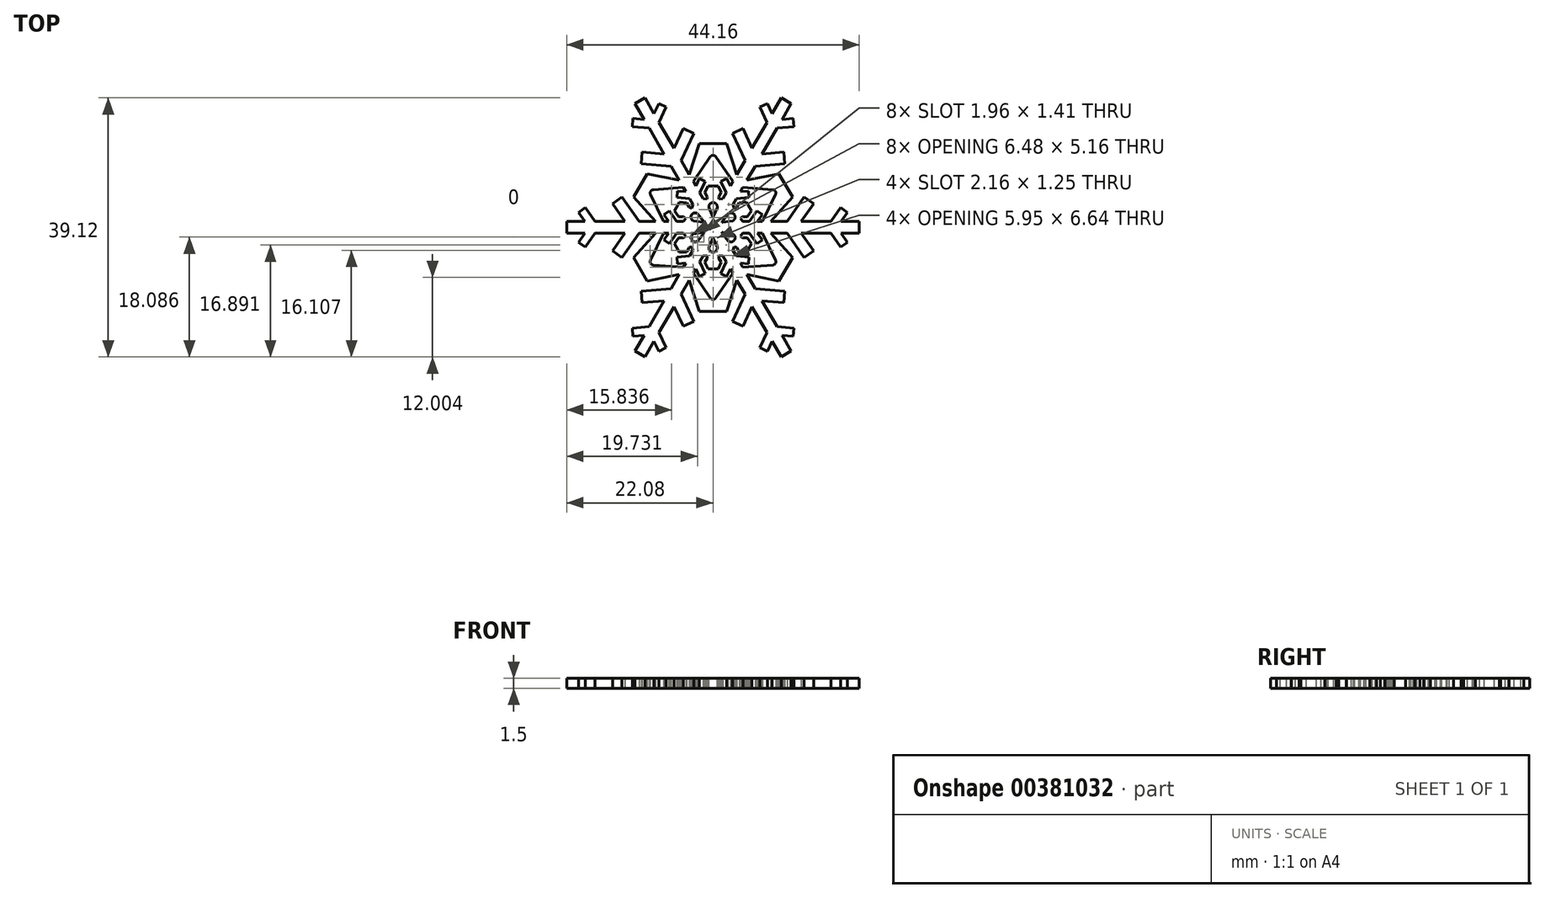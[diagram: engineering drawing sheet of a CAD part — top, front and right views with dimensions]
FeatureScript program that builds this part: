
annotation { "Feature Type Name" : "Feature", "Feature Type Description" : "" }
export const myFeature = defineFeature(function(context is Context, id is Id, definition is map)
    precondition{}
    {
        {
            var Q0;
            Q0=qCreatedBy(makeId("Top.planeOp"),FACE);
            var sketch = newSketch(context, id + "F0", { "sketchPlane" : qUnion([Q0])});
            skLineSegment(sketch, "E0.bottom", {"start": v(-43.7, 44.8) * mm, "end": v(41.1, 44.8) * mm});
            skLineSegment(sketch, "E0.top", {"start": v(-43.7, -40) * mm, "end": v(41.1, -40) * mm});
            skLineSegment(sketch, "E0.left", {"start": v(-43.7, 44.8) * mm, "end": v(-43.7, -40) * mm});
            skLineSegment(sketch, "E0.right", {"start": v(41.1, 44.8) * mm, "end": v(41.1, -40) * mm});
            skLineSegment(sketch, "E1", {"start": v(-44.15, 0) * mm, "end": v(-44.15, 1.75) * mm});
            skLineSegment(sketch, "E2", {"start": v(-44.15, 1.75) * mm, "end": v(-38.65, 1.75) * mm});
            skLineSegment(sketch, "E3", {"start": v(-38.65, 1.75) * mm, "end": v(-40.58, 4.5) * mm});
            skLineSegment(sketch, "E4", {"start": v(-40.58, 4.5) * mm, "end": v(-38.53, 5.94) * mm});
            skLineSegment(sketch, "E5", {"start": v(-38.53, 5.94) * mm, "end": v(-35.6, 1.75) * mm});
            skLineSegment(sketch, "E6", {"start": v(-35.6, 1.75) * mm, "end": v(-26.6, 1.75) * mm});
            skLineSegment(sketch, "E7", {"start": v(-26.6, 1.75) * mm, "end": v(-30.36, 7.13) * mm});
            skLineSegment(sketch, "E8", {"start": v(-30.36, 7.13) * mm, "end": v(-27.49, 9.13) * mm});
            skLineSegment(sketch, "E9", {"start": v(-27.49, 9.13) * mm, "end": v(-22.34, 1.75) * mm});
            skLineSegment(sketch, "E10", {"start": v(-22.34, 1.75) * mm, "end": v(-17.4, 1.75) * mm});
            skLineSegment(sketch, "E11", {"start": v(-14.94, 1.75) * mm, "end": v(-13.44, 1.75) * mm});
            skLineSegment(sketch, "E12", {"start": v(-13.44, 1.75) * mm, "end": v(-14.87, 3.8) * mm});
            skLineSegment(sketch, "E13", {"start": v(-14.87, 3.8) * mm, "end": v(-13.23, 4.94) * mm});
            skLineSegment(sketch, "E14", {"start": v(-13.23, 4.94) * mm, "end": v(-11, 1.75) * mm});
            skLineSegment(sketch, "E15", {"start": v(0, 0) * mm, "end": v(-44.15, 0) * mm, "construction": true});
            skLineSegment(sketch, "E16", {"start": v(-11, 1.75) * mm, "end": v(-8.98, 1.75) * mm});
            skLineSegment(sketch, "E17", {"start": v(0, 0) * mm, "end": v(-10.85, 6.27) * mm});
            skLineSegment(sketch, "E18", {"start": v(-8.98, 1.75) * mm, "end": v(-8.24, 2.67) * mm});
            skLineSegment(sketch, "E19", {"start": v(-8.24, 2.67) * mm, "end": v(-8.84, 3.15) * mm});
            skLineSegment(sketch, "E20", {"start": v(-8.84, 3.15) * mm, "end": v(-10.37, 3.15) * mm});
            skLineSegment(sketch, "E21", {"start": v(-10.37, 3.15) * mm, "end": v(-11.62, 4.94) * mm});
            skLineSegment(sketch, "E22", {"start": v(-11.62, 4.94) * mm, "end": v(-10.85, 6.27) * mm});
            skLineSegment(sketch, "E23", {"start": v(-10.85, 6.27) * mm, "end": v(-31.84, 18.38) * mm, "construction": true});
            skLineSegment(sketch, "E24", {"start": v(-23.98, 9.13) * mm, "end": v(-21.94, 12.67) * mm});
            skLineSegment(sketch, "E25", {"start": v(-14.94, 1.75) * mm, "end": v(-19.5, 11.26) * mm});
            skLineSegment(sketch, "E26", {"start": v(-23.98, 9.13) * mm, "end": v(-17.4, 1.75) * mm});
            skLineSegment(sketch, "E27", {"start": v(-21.94, 12.67) * mm, "end": v(-19.5, 11.26) * mm});
            skLineSegment(sketch, "E28.MirrorCS", {"start": v(0, 0) * mm, "end": v(-10.85, -6.27) * mm});
            skLineSegment(sketch, "E29.MirrorCS", {"start": v(-44.15, 0) * mm, "end": v(-44.15, -1.75) * mm});
            skLineSegment(sketch, "E30.MirrorCS", {"start": v(-14.94, -1.75) * mm, "end": v(-13.44, -1.75) * mm});
            skLineSegment(sketch, "E31.MirrorCS", {"start": v(-11.62, -4.94) * mm, "end": v(-10.85, -6.27) * mm});
            skLineSegment(sketch, "E32.MirrorCS", {"start": v(-14.87, -3.8) * mm, "end": v(-13.23, -4.94) * mm});
            skLineSegment(sketch, "E33.MirrorCS", {"start": v(-8.98, -1.75) * mm, "end": v(-8.24, -2.67) * mm});
            skLineSegment(sketch, "E34.MirrorCS", {"start": v(-8.84, -3.15) * mm, "end": v(-10.37, -3.15) * mm});
            skLineSegment(sketch, "E35.MirrorCS", {"start": v(-8.24, -2.67) * mm, "end": v(-8.84, -3.15) * mm});
            skLineSegment(sketch, "E36.MirrorCS", {"start": v(-14.94, -1.75) * mm, "end": v(-19.5, -11.26) * mm});
            skLineSegment(sketch, "E37.MirrorCS", {"start": v(-27.49, -9.13) * mm, "end": v(-22.34, -1.75) * mm});
            skLineSegment(sketch, "E38.MirrorCS", {"start": v(-21.94, -12.67) * mm, "end": v(-19.5, -11.26) * mm});
            skLineSegment(sketch, "E39.MirrorCS", {"start": v(-23.98, -9.13) * mm, "end": v(-21.94, -12.67) * mm});
            skLineSegment(sketch, "E40.MirrorCS", {"start": v(-11, -1.75) * mm, "end": v(-8.98, -1.75) * mm});
            skLineSegment(sketch, "E41.MirrorCS", {"start": v(-38.53, -5.94) * mm, "end": v(-35.6, -1.75) * mm});
            skLineSegment(sketch, "E42.MirrorCS", {"start": v(-40.58, -4.5) * mm, "end": v(-38.53, -5.94) * mm});
            skLineSegment(sketch, "E43.MirrorCS", {"start": v(-38.65, -1.75) * mm, "end": v(-40.58, -4.5) * mm});
            skLineSegment(sketch, "E44.MirrorCS", {"start": v(-44.15, -1.75) * mm, "end": v(-38.65, -1.75) * mm});
            skLineSegment(sketch, "E45.MirrorCS", {"start": v(-23.98, -9.13) * mm, "end": v(-17.4, -1.75) * mm});
            skLineSegment(sketch, "E46.MirrorCS", {"start": v(-30.36, -7.13) * mm, "end": v(-27.49, -9.13) * mm});
            skLineSegment(sketch, "E47.MirrorCS", {"start": v(-26.6, -1.75) * mm, "end": v(-30.36, -7.13) * mm});
            skLineSegment(sketch, "E48.MirrorCS", {"start": v(-35.6, -1.75) * mm, "end": v(-26.6, -1.75) * mm});
            skLineSegment(sketch, "E49.MirrorCS", {"start": v(-22.34, -1.75) * mm, "end": v(-17.4, -1.75) * mm});
            skLineSegment(sketch, "E50.MirrorCS", {"start": v(-13.44, -1.75) * mm, "end": v(-14.87, -3.8) * mm});
            skLineSegment(sketch, "E51.MirrorCS", {"start": v(-10.37, -3.15) * mm, "end": v(-11.62, -4.94) * mm});
            skLineSegment(sketch, "E52.MirrorCS", {"start": v(-13.23, -4.94) * mm, "end": v(-11, -1.75) * mm});
            skSolve(sketch);
        }
        {
            var Q0;
            Q0=makeQuery(id+"F0.imprint","IMPRINT",FACE,{"disambiguationData":[TD([[makeQuery(id+"F0.imprint","IMPRINT",EDGE,{"derivedFrom":sQuery(id+"F0.wireOp",EDGE,"E1")}),-1.0]])]});
            var Q1;
            {var subQ0=sQuery(id+"F0.wireOp",EDGE,"E3");Q1=makeQuery(id+"F0.imprint","IMPRINT",FACE,{"disambiguationData":[TD([[makeQuery(id+"F0.imprint","IMPRINT",EDGE,{"derivedFrom":subQ0}),-1.0]])]});}
            extrude(context, id + "F1", {"entities" : qUnion([Q0, Q1]), "endBound" : BoundingType.SYMMETRIC, "depth" : 3 * mm});
        }
        {
            var Q0;
            Q0=qCreatedBy(makeId("Right.planeOp"),FACE);
            var sketch = newSketch(context, id + "F2", { "sketchPlane" : qUnion([Q0])});
            skLineSegment(sketch, "E53", {"start": v(0, 0) * mm, "end": v(0, -43.45) * mm, "construction": true});
            skSolve(sketch);
        }
        {
            var Q0;
            Q0=makeQuery(id+"F1.opExtrude","SWEPT_BODY",BODY,{"disambiguationData":[OSD([sQuery(id+"F0.wireOp",EDGE,"E1"),sQuery(id+"F0.wireOp",EDGE,"E2"),sQuery(id+"F0.wireOp",EDGE,"E3"),sQuery(id+"F0.wireOp",EDGE,"E4"),sQuery(id+"F0.wireOp",EDGE,"E5"),sQuery(id+"F0.wireOp",EDGE,"E6"),sQuery(id+"F0.wireOp",EDGE,"E7"),sQuery(id+"F0.wireOp",EDGE,"E8"),sQuery(id+"F0.wireOp",EDGE,"E9"),sQuery(id+"F0.wireOp",EDGE,"E10"),sQuery(id+"F0.wireOp",EDGE,"189a7a4e-f39c-4bfd-b122-43a29ca94680"),sQuery(id+"F0.wireOp",EDGE,"67050dc1-3990-4a49-9707-dffdccfb30a0"),sQuery(id+"F0.wireOp",EDGE,"437a0215-fb6c-4063-ad75-b84b83856d58"),sQuery(id+"F0.wireOp",EDGE,"E11"),sQuery(id+"F0.wireOp",EDGE,"E12"),sQuery(id+"F0.wireOp",EDGE,"E13"),sQuery(id+"F0.wireOp",EDGE,"E14"),sQuery(id+"F0.wireOp",EDGE,"5e9898c1-a996-4e9f-834a-20b7154747a1"),sQuery(id+"F0.wireOp",EDGE,"4f175b08-8b9f-4015-be58-81c3dce13333"),sQuery(id+"F0.wireOp",EDGE,"3166d6ec-2b74-46b0-8a25-8ff819b97b050.MirrorCS"),sQuery(id+"F0.wireOp",EDGE,"3166d6ec-2b74-46b0-8a25-8ff819b97b051.MirrorCS"),sQuery(id+"F0.wireOp",EDGE,"3166d6ec-2b74-46b0-8a25-8ff819b97b052.MirrorCS"),sQuery(id+"F0.wireOp",EDGE,"3166d6ec-2b74-46b0-8a25-8ff819b97b053.MirrorCS"),sQuery(id+"F0.wireOp",EDGE,"3166d6ec-2b74-46b0-8a25-8ff819b97b054.MirrorCS"),sQuery(id+"F0.wireOp",EDGE,"3166d6ec-2b74-46b0-8a25-8ff819b97b055.MirrorCS"),sQuery(id+"F0.wireOp",EDGE,"3166d6ec-2b74-46b0-8a25-8ff819b97b056.MirrorCS"),sQuery(id+"F0.wireOp",EDGE,"3166d6ec-2b74-46b0-8a25-8ff819b97b057.MirrorCS"),sQuery(id+"F0.wireOp",EDGE,"3166d6ec-2b74-46b0-8a25-8ff819b97b058.MirrorCS"),sQuery(id+"F0.wireOp",EDGE,"3166d6ec-2b74-46b0-8a25-8ff819b97b059.MirrorCS"),sQuery(id+"F0.wireOp",EDGE,"3166d6ec-2b74-46b0-8a25-8ff819b97b0510.MirrorCS"),sQuery(id+"F0.wireOp",EDGE,"3166d6ec-2b74-46b0-8a25-8ff819b97b0511.MirrorCS"),sQuery(id+"F0.wireOp",EDGE,"3166d6ec-2b74-46b0-8a25-8ff819b97b0512.MirrorCS"),sQuery(id+"F0.wireOp",EDGE,"3166d6ec-2b74-46b0-8a25-8ff819b97b0513.MirrorCS"),sQuery(id+"F0.wireOp",EDGE,"3166d6ec-2b74-46b0-8a25-8ff819b97b0514.MirrorCS"),sQuery(id+"F0.wireOp",EDGE,"3166d6ec-2b74-46b0-8a25-8ff819b97b0515.MirrorCS"),sQuery(id+"F0.wireOp",EDGE,"3166d6ec-2b74-46b0-8a25-8ff819b97b0516.MirrorCS"),sQuery(id+"F0.wireOp",EDGE,"3166d6ec-2b74-46b0-8a25-8ff819b97b0517.MirrorCS"),sQuery(id+"F0.wireOp",EDGE,"3166d6ec-2b74-46b0-8a25-8ff819b97b0518.MirrorCS")])]});
            var Q1;
            Q1=sQuery(id+"F2.wireOp",EDGE,"E53");
            circularPattern(context, id + "F3", {"operationType" : NewBodyOperationType.ADD, "entities" : qUnion([Q0]), "axis" : qUnion([Q1]), "angle" : 60 * degree, "instanceCount" : 6});
        }
        {
            var Q0;
            {var subQ0=makeQuery(id+"F1.opExtrude","CAP_FACE",FACE,{"disambiguationData":[OSD([sQuery(id+"F0.wireOp",EDGE,"E1"),sQuery(id+"F0.wireOp",EDGE,"E2"),sQuery(id+"F0.wireOp",EDGE,"E3"),sQuery(id+"F0.wireOp",EDGE,"E4"),sQuery(id+"F0.wireOp",EDGE,"E5"),sQuery(id+"F0.wireOp",EDGE,"E6"),sQuery(id+"F0.wireOp",EDGE,"E7"),sQuery(id+"F0.wireOp",EDGE,"E8"),sQuery(id+"F0.wireOp",EDGE,"E9"),sQuery(id+"F0.wireOp",EDGE,"E10"),sQuery(id+"F0.wireOp",EDGE,"189a7a4e-f39c-4bfd-b122-43a29ca94680"),sQuery(id+"F0.wireOp",EDGE,"67050dc1-3990-4a49-9707-dffdccfb30a0"),sQuery(id+"F0.wireOp",EDGE,"437a0215-fb6c-4063-ad75-b84b83856d58"),sQuery(id+"F0.wireOp",EDGE,"E11"),sQuery(id+"F0.wireOp",EDGE,"E12"),sQuery(id+"F0.wireOp",EDGE,"E13"),sQuery(id+"F0.wireOp",EDGE,"E14"),sQuery(id+"F0.wireOp",EDGE,"E16"),sQuery(id+"F0.wireOp",EDGE,"E17"),sQuery(id+"F0.wireOp",EDGE,"E18"),sQuery(id+"F0.wireOp",EDGE,"E19"),sQuery(id+"F0.wireOp",EDGE,"E20"),sQuery(id+"F0.wireOp",EDGE,"E21"),sQuery(id+"F0.wireOp",EDGE,"E22"),sQuery(id+"F0.wireOp",EDGE,"0c32c283-354d-45ec-8926-575daeb4bd260.MirrorCS"),sQuery(id+"F0.wireOp",EDGE,"0c32c283-354d-45ec-8926-575daeb4bd261.MirrorCS"),sQuery(id+"F0.wireOp",EDGE,"0c32c283-354d-45ec-8926-575daeb4bd262.MirrorCS"),sQuery(id+"F0.wireOp",EDGE,"0c32c283-354d-45ec-8926-575daeb4bd263.MirrorCS"),sQuery(id+"F0.wireOp",EDGE,"0c32c283-354d-45ec-8926-575daeb4bd264.MirrorCS"),sQuery(id+"F0.wireOp",EDGE,"0c32c283-354d-45ec-8926-575daeb4bd265.MirrorCS"),sQuery(id+"F0.wireOp",EDGE,"0c32c283-354d-45ec-8926-575daeb4bd266.MirrorCS"),sQuery(id+"F0.wireOp",EDGE,"0c32c283-354d-45ec-8926-575daeb4bd267.MirrorCS"),sQuery(id+"F0.wireOp",EDGE,"0c32c283-354d-45ec-8926-575daeb4bd268.MirrorCS"),sQuery(id+"F0.wireOp",EDGE,"0c32c283-354d-45ec-8926-575daeb4bd269.MirrorCS"),sQuery(id+"F0.wireOp",EDGE,"0c32c283-354d-45ec-8926-575daeb4bd2610.MirrorCS"),sQuery(id+"F0.wireOp",EDGE,"0c32c283-354d-45ec-8926-575daeb4bd2611.MirrorCS"),sQuery(id+"F0.wireOp",EDGE,"0c32c283-354d-45ec-8926-575daeb4bd2612.MirrorCS"),sQuery(id+"F0.wireOp",EDGE,"0c32c283-354d-45ec-8926-575daeb4bd2613.MirrorCS"),sQuery(id+"F0.wireOp",EDGE,"0c32c283-354d-45ec-8926-575daeb4bd2614.MirrorCS"),sQuery(id+"F0.wireOp",EDGE,"0c32c283-354d-45ec-8926-575daeb4bd2615.MirrorCS"),sQuery(id+"F0.wireOp",EDGE,"0c32c283-354d-45ec-8926-575daeb4bd2616.MirrorCS"),sQuery(id+"F0.wireOp",EDGE,"0c32c283-354d-45ec-8926-575daeb4bd2617.MirrorCS"),sQuery(id+"F0.wireOp",EDGE,"0c32c283-354d-45ec-8926-575daeb4bd2618.MirrorCS"),sQuery(id+"F0.wireOp",EDGE,"0c32c283-354d-45ec-8926-575daeb4bd2619.MirrorCS"),sQuery(id+"F0.wireOp",EDGE,"0c32c283-354d-45ec-8926-575daeb4bd2620.MirrorCS"),sQuery(id+"F0.wireOp",EDGE,"0c32c283-354d-45ec-8926-575daeb4bd2621.MirrorCS"),sQuery(id+"F0.wireOp",EDGE,"0c32c283-354d-45ec-8926-575daeb4bd2622.MirrorCS"),sQuery(id+"F0.wireOp",EDGE,"0c32c283-354d-45ec-8926-575daeb4bd2623.MirrorCS")])],"isStart":false});Q0=makeQuery(id+"F3.boolean.opBoolean","MERGE",FACE,{"derivedFrom":[subQ0,makeQuery(id+"F3.opPattern","COPY",FACE,{"derivedFrom":subQ0,"instanceName":"1"}),makeQuery(id+"F3.opPattern","COPY",FACE,{"derivedFrom":subQ0,"instanceName":"2"}),makeQuery(id+"F3.opPattern","COPY",FACE,{"derivedFrom":subQ0,"instanceName":"3"}),makeQuery(id+"F3.opPattern","COPY",FACE,{"derivedFrom":subQ0,"instanceName":"4"}),makeQuery(id+"F3.opPattern","COPY",FACE,{"derivedFrom":subQ0,"instanceName":"5"})]});}
            var sketch = newSketch(context, id + "F4", { "sketchPlane" : qUnion([Q0])});
            skLineSegment(sketch, "E54", {"start": v(0, 0) * mm, "end": v(-10.85, 6.27) * mm, "construction": true});
            skLineSegment(sketch, "E55", {"start": v(-6.5, 3.75) * mm, "end": v(-2.6, 1.5) * mm, "construction": true});
            skLineSegment(sketch, "E56", {"start": v(-5.87, 1.94) * mm, "end": v(-2.6, 1.5) * mm});
            skLineSegment(sketch, "E57.MirrorCS", {"start": v(-4.62, 4.1) * mm, "end": v(-2.6, 1.5) * mm});
            skLineSegment(sketch, "E58", {"start": v(-5.87, 1.94) * mm, "end": v(-4.62, 4.1) * mm, "construction": true});
            skArc(sketch, "E59", {"start": v(-4.62, 4.1) * mm, "mid": v(-6.5, 3.75) * mm, "end": v(-5.87, 1.94) * mm});
            skSolve(sketch);
        }
        {
            var Q0;
            Q0=makeQuery(id+"F4.imprint","IMPRINT",FACE,{"disambiguationData":[TD([[makeQuery(id+"F4.imprint","IMPRINT",EDGE,{"derivedFrom":sQuery(id+"F4.wireOp",EDGE,"980073ca-cf30-472a-b92e-9ee7ff5da41c")}),1.0]])]});
            var Q1;
            Q1=makeQuery(id+"F4.imprint","IMPRINT",FACE,{"disambiguationData":[TD([[makeQuery(id+"F4.imprint","IMPRINT",EDGE,{"derivedFrom":sQuery(id+"F4.wireOp",EDGE,"E56")}),1.0]])]});
            extrude(context, id + "F5", {"entities" : qUnion([Q0, Q1]), "operationType" : NewBodyOperationType.REMOVE, "endBound" : BoundingType.UP_TO_NEXT, "oppositeDirection" : true, "depth" : 25 * mm});
        }
        {
            var Q0;
            Q0=makeQuery(id+"F5.boolean.opBoolean","COPY",EDGE,{"derivedFrom":makeQuery(id+"F5.opExtrude","SWEPT_EDGE",EDGE,{"disambiguationData":[OSD([sQuery(id+"F4.wireOp",EDGE,"E56"),sQuery(id+"F4.wireOp",EDGE,"E57.MirrorCS")])]})});
            fillet(context, id + "F6", {"entities" : qUnion([Q0]), "radius" : 0.1 * mm, "tangentPropagation" : true, "allowEdgeOverflow" : false});
        }
        {
            var Q0;
            Q0=makeQuery(id+"F5.boolean.opBoolean","COPY",FACE,{"derivedFrom":makeQuery(id+"F5.opExtrude","SWEPT_FACE",FACE,{"disambiguationData":[OSD([sQuery(id+"F4.wireOp",EDGE,"E59")])]})});
            var Q1;
            Q1=makeQuery(id+"F5.boolean.opBoolean","COPY",FACE,{"derivedFrom":makeQuery(id+"F5.opExtrude","SWEPT_FACE",FACE,{"disambiguationData":[OSD([sQuery(id+"F4.wireOp",EDGE,"E56")])]})});
            var Q2;
            Q2=makeQuery(id+"F5.boolean.opBoolean","COPY",FACE,{"derivedFrom":makeQuery(id+"F5.opExtrude","SWEPT_FACE",FACE,{"disambiguationData":[OSD([sQuery(id+"F4.wireOp",EDGE,"E57.MirrorCS")])]})});
            var Q3;
            Q3=makeQuery(id+"F6.opFillet","BLEND_FACE",FACE,{"disambiguationData":[OSD([sQuery(id+"F4.wireOp",EDGE,"E56"),sQuery(id+"F4.wireOp",EDGE,"E57.MirrorCS")])]});
            var Q4;
            Q4=sQuery(id+"F2.wireOp",EDGE,"E53");
            circularPattern(context, id + "F7", {"faces" : qUnion([Q0, Q1, Q2, Q3]), "axis" : qUnion([Q4]), "angle" : 60 * degree, "instanceCount" : 6, "patternType" : PatternType.FACE});
        }
        {
            var Q0;
            {var subQ0=makeQuery(id+"F1.opExtrude","CAP_FACE",FACE,{"disambiguationData":[OSD([sQuery(id+"F0.wireOp",EDGE,"E1"),sQuery(id+"F0.wireOp",EDGE,"E2"),sQuery(id+"F0.wireOp",EDGE,"E3"),sQuery(id+"F0.wireOp",EDGE,"E4"),sQuery(id+"F0.wireOp",EDGE,"E5"),sQuery(id+"F0.wireOp",EDGE,"E6"),sQuery(id+"F0.wireOp",EDGE,"E7"),sQuery(id+"F0.wireOp",EDGE,"E8"),sQuery(id+"F0.wireOp",EDGE,"E9"),sQuery(id+"F0.wireOp",EDGE,"E10"),sQuery(id+"F0.wireOp",EDGE,"189a7a4e-f39c-4bfd-b122-43a29ca94680"),sQuery(id+"F0.wireOp",EDGE,"67050dc1-3990-4a49-9707-dffdccfb30a0"),sQuery(id+"F0.wireOp",EDGE,"437a0215-fb6c-4063-ad75-b84b83856d58"),sQuery(id+"F0.wireOp",EDGE,"E11"),sQuery(id+"F0.wireOp",EDGE,"E12"),sQuery(id+"F0.wireOp",EDGE,"E13"),sQuery(id+"F0.wireOp",EDGE,"E14"),sQuery(id+"F0.wireOp",EDGE,"E16"),sQuery(id+"F0.wireOp",EDGE,"E17"),sQuery(id+"F0.wireOp",EDGE,"E18"),sQuery(id+"F0.wireOp",EDGE,"E19"),sQuery(id+"F0.wireOp",EDGE,"E20"),sQuery(id+"F0.wireOp",EDGE,"E21"),sQuery(id+"F0.wireOp",EDGE,"E22"),sQuery(id+"F0.wireOp",EDGE,"0c32c283-354d-45ec-8926-575daeb4bd260.MirrorCS"),sQuery(id+"F0.wireOp",EDGE,"0c32c283-354d-45ec-8926-575daeb4bd261.MirrorCS"),sQuery(id+"F0.wireOp",EDGE,"0c32c283-354d-45ec-8926-575daeb4bd262.MirrorCS"),sQuery(id+"F0.wireOp",EDGE,"0c32c283-354d-45ec-8926-575daeb4bd263.MirrorCS"),sQuery(id+"F0.wireOp",EDGE,"0c32c283-354d-45ec-8926-575daeb4bd264.MirrorCS"),sQuery(id+"F0.wireOp",EDGE,"0c32c283-354d-45ec-8926-575daeb4bd265.MirrorCS"),sQuery(id+"F0.wireOp",EDGE,"0c32c283-354d-45ec-8926-575daeb4bd266.MirrorCS"),sQuery(id+"F0.wireOp",EDGE,"0c32c283-354d-45ec-8926-575daeb4bd267.MirrorCS"),sQuery(id+"F0.wireOp",EDGE,"0c32c283-354d-45ec-8926-575daeb4bd268.MirrorCS"),sQuery(id+"F0.wireOp",EDGE,"0c32c283-354d-45ec-8926-575daeb4bd269.MirrorCS"),sQuery(id+"F0.wireOp",EDGE,"0c32c283-354d-45ec-8926-575daeb4bd2610.MirrorCS"),sQuery(id+"F0.wireOp",EDGE,"0c32c283-354d-45ec-8926-575daeb4bd2611.MirrorCS"),sQuery(id+"F0.wireOp",EDGE,"0c32c283-354d-45ec-8926-575daeb4bd2612.MirrorCS"),sQuery(id+"F0.wireOp",EDGE,"0c32c283-354d-45ec-8926-575daeb4bd2613.MirrorCS"),sQuery(id+"F0.wireOp",EDGE,"0c32c283-354d-45ec-8926-575daeb4bd2614.MirrorCS"),sQuery(id+"F0.wireOp",EDGE,"0c32c283-354d-45ec-8926-575daeb4bd2615.MirrorCS"),sQuery(id+"F0.wireOp",EDGE,"0c32c283-354d-45ec-8926-575daeb4bd2616.MirrorCS"),sQuery(id+"F0.wireOp",EDGE,"0c32c283-354d-45ec-8926-575daeb4bd2617.MirrorCS"),sQuery(id+"F0.wireOp",EDGE,"0c32c283-354d-45ec-8926-575daeb4bd2618.MirrorCS"),sQuery(id+"F0.wireOp",EDGE,"0c32c283-354d-45ec-8926-575daeb4bd2619.MirrorCS"),sQuery(id+"F0.wireOp",EDGE,"0c32c283-354d-45ec-8926-575daeb4bd2620.MirrorCS"),sQuery(id+"F0.wireOp",EDGE,"0c32c283-354d-45ec-8926-575daeb4bd2621.MirrorCS"),sQuery(id+"F0.wireOp",EDGE,"0c32c283-354d-45ec-8926-575daeb4bd2622.MirrorCS"),sQuery(id+"F0.wireOp",EDGE,"0c32c283-354d-45ec-8926-575daeb4bd2623.MirrorCS")])],"isStart":false});Q0=makeQuery(id+"F3.boolean.opBoolean","MERGE",FACE,{"derivedFrom":[subQ0,makeQuery(id+"F3.opPattern","COPY",FACE,{"derivedFrom":subQ0,"instanceName":"1"}),makeQuery(id+"F3.opPattern","COPY",FACE,{"derivedFrom":subQ0,"instanceName":"2"}),makeQuery(id+"F3.opPattern","COPY",FACE,{"derivedFrom":subQ0,"instanceName":"3"}),makeQuery(id+"F3.opPattern","COPY",FACE,{"derivedFrom":subQ0,"instanceName":"4"}),makeQuery(id+"F3.opPattern","COPY",FACE,{"derivedFrom":subQ0,"instanceName":"5"})]});}
            var sketch = newSketch(context, id + "F8", { "sketchPlane" : qUnion([Q0])});
            skArc(sketch, "E60", {"start": v(-44.15, 1.75) * mm, "mid": v(-51.75, 0) * mm, "end": v(-44.15, -1.75) * mm});
            skCircle(sketch, "E61", {"center": v(-47.75, 0) * mm, "radius": 2 * mm});
            skSolve(sketch);
        }
        {
            var Q0;
            Q0=makeQuery(id+"F8.imprint","IMPRINT",FACE,{"disambiguationData":[TD([[makeQuery(id+"F8.imprint","IMPRINT",EDGE,{"derivedFrom":sQuery(id+"F8.wireOp",EDGE,"E60")}),1.0]])]});
            extrude(context, id + "F9", {"entities" : qUnion([Q0]), "operationType" : NewBodyOperationType.ADD, "oppositeDirection" : true, "depth" : 3 * mm});
        }
        {
            var Q0;
            Q0=makeQuery(id+"F3.boolean.opBoolean","MERGE",EDGE,{"derivedFrom":[makeQuery(id+"F1.opExtrude","SWEPT_EDGE",EDGE,{"disambiguationData":[OSD([sQuery(id+"F0.wireOp",EDGE,"E25"),sQuery(id+"F0.wireOp",EDGE,"E27")])]}),makeQuery(id+"F3.opPattern","COPY",EDGE,{"derivedFrom":makeQuery(id+"F1.opExtrude","SWEPT_EDGE",EDGE,{"disambiguationData":[OSD([sQuery(id+"F0.wireOp",EDGE,"E36.MirrorCS"),sQuery(id+"F0.wireOp",EDGE,"E38.MirrorCS")])]}),"instanceName":"1"})]});
            var Q1;
            Q1=makeQuery(id+"F3.boolean.opBoolean","MERGE",EDGE,{"derivedFrom":[makeQuery(id+"F1.opExtrude","SWEPT_EDGE",EDGE,{"disambiguationData":[OSD([sQuery(id+"F0.wireOp",EDGE,"E36.MirrorCS"),sQuery(id+"F0.wireOp",EDGE,"E38.MirrorCS")])]}),makeQuery(id+"F3.opPattern","COPY",EDGE,{"derivedFrom":makeQuery(id+"F1.opExtrude","SWEPT_EDGE",EDGE,{"disambiguationData":[OSD([sQuery(id+"F0.wireOp",EDGE,"E25"),sQuery(id+"F0.wireOp",EDGE,"E27")])]}),"instanceName":"5"})]});
            var Q2;
            Q2=makeQuery(id+"F3.boolean.opBoolean","MERGE",EDGE,{"derivedFrom":[makeQuery(id+"F3.opPattern","COPY",EDGE,{"derivedFrom":makeQuery(id+"F1.opExtrude","SWEPT_EDGE",EDGE,{"disambiguationData":[OSD([sQuery(id+"F0.wireOp",EDGE,"E25"),sQuery(id+"F0.wireOp",EDGE,"E27")])]}),"instanceName":"4"}),makeQuery(id+"F3.opPattern","COPY",EDGE,{"derivedFrom":makeQuery(id+"F1.opExtrude","SWEPT_EDGE",EDGE,{"disambiguationData":[OSD([sQuery(id+"F0.wireOp",EDGE,"E36.MirrorCS"),sQuery(id+"F0.wireOp",EDGE,"E38.MirrorCS")])]}),"instanceName":"5"})]});
            var Q3;
            Q3=makeQuery(id+"F3.boolean.opBoolean","MERGE",EDGE,{"derivedFrom":[makeQuery(id+"F3.opPattern","COPY",EDGE,{"derivedFrom":makeQuery(id+"F1.opExtrude","SWEPT_EDGE",EDGE,{"disambiguationData":[OSD([sQuery(id+"F0.wireOp",EDGE,"E25"),sQuery(id+"F0.wireOp",EDGE,"E27")])]}),"instanceName":"3"}),makeQuery(id+"F3.opPattern","COPY",EDGE,{"derivedFrom":makeQuery(id+"F1.opExtrude","SWEPT_EDGE",EDGE,{"disambiguationData":[OSD([sQuery(id+"F0.wireOp",EDGE,"E36.MirrorCS"),sQuery(id+"F0.wireOp",EDGE,"E38.MirrorCS")])]}),"instanceName":"4"})]});
            var Q4;
            Q4=makeQuery(id+"F3.boolean.opBoolean","MERGE",EDGE,{"derivedFrom":[makeQuery(id+"F3.opPattern","COPY",EDGE,{"derivedFrom":makeQuery(id+"F1.opExtrude","SWEPT_EDGE",EDGE,{"disambiguationData":[OSD([sQuery(id+"F0.wireOp",EDGE,"E25"),sQuery(id+"F0.wireOp",EDGE,"E27")])]}),"instanceName":"1"}),makeQuery(id+"F3.opPattern","COPY",EDGE,{"derivedFrom":makeQuery(id+"F1.opExtrude","SWEPT_EDGE",EDGE,{"disambiguationData":[OSD([sQuery(id+"F0.wireOp",EDGE,"E36.MirrorCS"),sQuery(id+"F0.wireOp",EDGE,"E38.MirrorCS")])]}),"instanceName":"2"})]});
            var Q5;
            Q5=makeQuery(id+"F3.boolean.opBoolean","MERGE",EDGE,{"derivedFrom":[makeQuery(id+"F3.opPattern","COPY",EDGE,{"derivedFrom":makeQuery(id+"F1.opExtrude","SWEPT_EDGE",EDGE,{"disambiguationData":[OSD([sQuery(id+"F0.wireOp",EDGE,"E25"),sQuery(id+"F0.wireOp",EDGE,"E27")])]}),"instanceName":"2"}),makeQuery(id+"F3.opPattern","COPY",EDGE,{"derivedFrom":makeQuery(id+"F1.opExtrude","SWEPT_EDGE",EDGE,{"disambiguationData":[OSD([sQuery(id+"F0.wireOp",EDGE,"E36.MirrorCS"),sQuery(id+"F0.wireOp",EDGE,"E38.MirrorCS")])]}),"instanceName":"3"})]});
            fillet(context, id + "F10", {"entities" : qUnion([Q0, Q1, Q2, Q3, Q4, Q5]), "radius" : 1 * mm, "tangentPropagation" : true, "allowEdgeOverflow" : false});
        }
        {
            var Q0;
            {var subQ0=sQuery(id+"F0.wireOp",EDGE,"E29.MirrorCS");var subQ1=sQuery(id+"F0.wireOp",EDGE,"E1");var subQ2=makeQuery(id+"F1.opExtrude","CAP_FACE",FACE,{"disambiguationData":[OSD([subQ1,sQuery(id+"F0.wireOp",EDGE,"E2"),sQuery(id+"F0.wireOp",EDGE,"E3"),sQuery(id+"F0.wireOp",EDGE,"E4"),sQuery(id+"F0.wireOp",EDGE,"E5"),sQuery(id+"F0.wireOp",EDGE,"E6"),sQuery(id+"F0.wireOp",EDGE,"E7"),sQuery(id+"F0.wireOp",EDGE,"E8"),sQuery(id+"F0.wireOp",EDGE,"E9"),sQuery(id+"F0.wireOp",EDGE,"E10"),sQuery(id+"F0.wireOp",EDGE,"E11"),sQuery(id+"F0.wireOp",EDGE,"E12"),sQuery(id+"F0.wireOp",EDGE,"E13"),sQuery(id+"F0.wireOp",EDGE,"E14"),sQuery(id+"F0.wireOp",EDGE,"E16"),sQuery(id+"F0.wireOp",EDGE,"E17"),sQuery(id+"F0.wireOp",EDGE,"E18"),sQuery(id+"F0.wireOp",EDGE,"E19"),sQuery(id+"F0.wireOp",EDGE,"E20"),sQuery(id+"F0.wireOp",EDGE,"E21"),sQuery(id+"F0.wireOp",EDGE,"E22"),sQuery(id+"F0.wireOp",EDGE,"E24"),sQuery(id+"F0.wireOp",EDGE,"E25"),sQuery(id+"F0.wireOp",EDGE,"E26"),sQuery(id+"F0.wireOp",EDGE,"E27"),sQuery(id+"F0.wireOp",EDGE,"E28.MirrorCS"),subQ0,sQuery(id+"F0.wireOp",EDGE,"E30.MirrorCS"),sQuery(id+"F0.wireOp",EDGE,"E31.MirrorCS"),sQuery(id+"F0.wireOp",EDGE,"E32.MirrorCS"),sQuery(id+"F0.wireOp",EDGE,"E33.MirrorCS"),sQuery(id+"F0.wireOp",EDGE,"E34.MirrorCS"),sQuery(id+"F0.wireOp",EDGE,"E35.MirrorCS"),sQuery(id+"F0.wireOp",EDGE,"E36.MirrorCS"),sQuery(id+"F0.wireOp",EDGE,"E37.MirrorCS"),sQuery(id+"F0.wireOp",EDGE,"E38.MirrorCS"),sQuery(id+"F0.wireOp",EDGE,"E39.MirrorCS"),sQuery(id+"F0.wireOp",EDGE,"E40.MirrorCS"),sQuery(id+"F0.wireOp",EDGE,"E41.MirrorCS"),sQuery(id+"F0.wireOp",EDGE,"E42.MirrorCS"),sQuery(id+"F0.wireOp",EDGE,"E43.MirrorCS"),sQuery(id+"F0.wireOp",EDGE,"E44.MirrorCS"),sQuery(id+"F0.wireOp",EDGE,"E45.MirrorCS"),sQuery(id+"F0.wireOp",EDGE,"E46.MirrorCS"),sQuery(id+"F0.wireOp",EDGE,"E47.MirrorCS"),sQuery(id+"F0.wireOp",EDGE,"E48.MirrorCS"),sQuery(id+"F0.wireOp",EDGE,"E49.MirrorCS"),sQuery(id+"F0.wireOp",EDGE,"E50.MirrorCS"),sQuery(id+"F0.wireOp",EDGE,"E51.MirrorCS"),sQuery(id+"F0.wireOp",EDGE,"E52.MirrorCS")])],"isStart":false});Q0=makeQuery(id+"F9.boolean.opBoolean","MERGE",FACE,{"derivedFrom":[makeQuery(id+"F3.boolean.opBoolean","MERGE",FACE,{"derivedFrom":[subQ2,makeQuery(id+"F3.opPattern","COPY",FACE,{"derivedFrom":subQ2,"instanceName":"1"}),makeQuery(id+"F3.opPattern","COPY",FACE,{"derivedFrom":subQ2,"instanceName":"2"}),makeQuery(id+"F3.opPattern","COPY",FACE,{"derivedFrom":subQ2,"instanceName":"3"}),makeQuery(id+"F3.opPattern","COPY",FACE,{"derivedFrom":subQ2,"instanceName":"4"}),makeQuery(id+"F3.opPattern","COPY",FACE,{"derivedFrom":subQ2,"instanceName":"5"})]}),makeQuery(id+"F9.opExtrude","CAP_FACE",FACE,{"disambiguationData":[OSD([subQ1,subQ0,sQuery(id+"F8.wireOp",EDGE,"E60"),sQuery(id+"F8.wireOp",EDGE,"E61")])],"isStart":true})]});}
            var sketch = newSketch(context, id + "F11", { "sketchPlane" : qUnion([Q0])});
            skLineSegment(sketch, "E62", {"start": v(-44.15, -1.75) * mm, "end": v(-44.15, 1.75) * mm});
            skSolve(sketch);
        }
        {
            var Q0;
            Q0=makeQuery(id+"F11.imprint","IMPRINT",FACE,{"disambiguationData":[TD([[makeQuery(id+"F11.imprint","IMPRINT",EDGE,{"derivedFrom":sQuery(id+"F11.wireOp",EDGE,"E62")}),1.0]])]});
            extrude(context, id + "F12", {"entities" : qUnion([Q0]), "operationType" : NewBodyOperationType.REMOVE, "oppositeDirection" : true, "depth" : 25 * mm});
        }
        {
            var Q0;
            Q0=makeQuery(id+"F1.opExtrude","SWEPT_BODY",BODY,{"disambiguationData":[OSD([sQuery(id+"F0.wireOp",EDGE,"E1"),sQuery(id+"F0.wireOp",EDGE,"E2"),sQuery(id+"F0.wireOp",EDGE,"E3"),sQuery(id+"F0.wireOp",EDGE,"E4"),sQuery(id+"F0.wireOp",EDGE,"E5"),sQuery(id+"F0.wireOp",EDGE,"E6"),sQuery(id+"F0.wireOp",EDGE,"E7"),sQuery(id+"F0.wireOp",EDGE,"E8"),sQuery(id+"F0.wireOp",EDGE,"E9"),sQuery(id+"F0.wireOp",EDGE,"E10"),sQuery(id+"F0.wireOp",EDGE,"E11"),sQuery(id+"F0.wireOp",EDGE,"E12"),sQuery(id+"F0.wireOp",EDGE,"E13"),sQuery(id+"F0.wireOp",EDGE,"E14"),sQuery(id+"F0.wireOp",EDGE,"E16"),sQuery(id+"F0.wireOp",EDGE,"E17"),sQuery(id+"F0.wireOp",EDGE,"E18"),sQuery(id+"F0.wireOp",EDGE,"E19"),sQuery(id+"F0.wireOp",EDGE,"E20"),sQuery(id+"F0.wireOp",EDGE,"E21"),sQuery(id+"F0.wireOp",EDGE,"E22"),sQuery(id+"F0.wireOp",EDGE,"E24"),sQuery(id+"F0.wireOp",EDGE,"E25"),sQuery(id+"F0.wireOp",EDGE,"E26"),sQuery(id+"F0.wireOp",EDGE,"E27"),sQuery(id+"F0.wireOp",EDGE,"E28.MirrorCS"),sQuery(id+"F0.wireOp",EDGE,"E29.MirrorCS"),sQuery(id+"F0.wireOp",EDGE,"E30.MirrorCS"),sQuery(id+"F0.wireOp",EDGE,"E31.MirrorCS"),sQuery(id+"F0.wireOp",EDGE,"E32.MirrorCS"),sQuery(id+"F0.wireOp",EDGE,"E33.MirrorCS"),sQuery(id+"F0.wireOp",EDGE,"E34.MirrorCS"),sQuery(id+"F0.wireOp",EDGE,"E35.MirrorCS"),sQuery(id+"F0.wireOp",EDGE,"E36.MirrorCS"),sQuery(id+"F0.wireOp",EDGE,"E37.MirrorCS"),sQuery(id+"F0.wireOp",EDGE,"E38.MirrorCS"),sQuery(id+"F0.wireOp",EDGE,"E39.MirrorCS"),sQuery(id+"F0.wireOp",EDGE,"E40.MirrorCS"),sQuery(id+"F0.wireOp",EDGE,"E41.MirrorCS"),sQuery(id+"F0.wireOp",EDGE,"E42.MirrorCS"),sQuery(id+"F0.wireOp",EDGE,"E43.MirrorCS"),sQuery(id+"F0.wireOp",EDGE,"E44.MirrorCS"),sQuery(id+"F0.wireOp",EDGE,"E45.MirrorCS"),sQuery(id+"F0.wireOp",EDGE,"E46.MirrorCS"),sQuery(id+"F0.wireOp",EDGE,"E47.MirrorCS"),sQuery(id+"F0.wireOp",EDGE,"E48.MirrorCS"),sQuery(id+"F0.wireOp",EDGE,"E49.MirrorCS"),sQuery(id+"F0.wireOp",EDGE,"E50.MirrorCS"),sQuery(id+"F0.wireOp",EDGE,"E51.MirrorCS"),sQuery(id+"F0.wireOp",EDGE,"E52.MirrorCS")])]});
            var Q1;
            Q1=sQuery(id+"F2.wireOp",VERTEX,"E53.start");
            transform(context, id + "F13", {"entities" : qUnion([Q0]), "transformType" : TransformType.SCALE_UNIFORMLY, "scale" : .5, "scalePoint" : qUnion([Q1]), "makeCopy" : false});
        }
        {
            var Q0;
            Q0=makeQuery(id+"F1.opExtrude","SWEPT_BODY",BODY,{"disambiguationData":[OSD([sQuery(id+"F0.wireOp",EDGE,"E1"),sQuery(id+"F0.wireOp",EDGE,"E2"),sQuery(id+"F0.wireOp",EDGE,"E3"),sQuery(id+"F0.wireOp",EDGE,"E4"),sQuery(id+"F0.wireOp",EDGE,"E5"),sQuery(id+"F0.wireOp",EDGE,"E6"),sQuery(id+"F0.wireOp",EDGE,"E7"),sQuery(id+"F0.wireOp",EDGE,"E8"),sQuery(id+"F0.wireOp",EDGE,"E9"),sQuery(id+"F0.wireOp",EDGE,"E10"),sQuery(id+"F0.wireOp",EDGE,"E11"),sQuery(id+"F0.wireOp",EDGE,"E12"),sQuery(id+"F0.wireOp",EDGE,"E13"),sQuery(id+"F0.wireOp",EDGE,"E14"),sQuery(id+"F0.wireOp",EDGE,"E16"),sQuery(id+"F0.wireOp",EDGE,"E17"),sQuery(id+"F0.wireOp",EDGE,"E18"),sQuery(id+"F0.wireOp",EDGE,"E19"),sQuery(id+"F0.wireOp",EDGE,"E20"),sQuery(id+"F0.wireOp",EDGE,"E21"),sQuery(id+"F0.wireOp",EDGE,"E22"),sQuery(id+"F0.wireOp",EDGE,"E24"),sQuery(id+"F0.wireOp",EDGE,"E25"),sQuery(id+"F0.wireOp",EDGE,"E26"),sQuery(id+"F0.wireOp",EDGE,"E27"),sQuery(id+"F0.wireOp",EDGE,"E28.MirrorCS"),sQuery(id+"F0.wireOp",EDGE,"E29.MirrorCS"),sQuery(id+"F0.wireOp",EDGE,"E30.MirrorCS"),sQuery(id+"F0.wireOp",EDGE,"E31.MirrorCS"),sQuery(id+"F0.wireOp",EDGE,"E32.MirrorCS"),sQuery(id+"F0.wireOp",EDGE,"E33.MirrorCS"),sQuery(id+"F0.wireOp",EDGE,"E34.MirrorCS"),sQuery(id+"F0.wireOp",EDGE,"E35.MirrorCS"),sQuery(id+"F0.wireOp",EDGE,"E36.MirrorCS"),sQuery(id+"F0.wireOp",EDGE,"E37.MirrorCS"),sQuery(id+"F0.wireOp",EDGE,"E38.MirrorCS"),sQuery(id+"F0.wireOp",EDGE,"E39.MirrorCS"),sQuery(id+"F0.wireOp",EDGE,"E40.MirrorCS"),sQuery(id+"F0.wireOp",EDGE,"E41.MirrorCS"),sQuery(id+"F0.wireOp",EDGE,"E42.MirrorCS"),sQuery(id+"F0.wireOp",EDGE,"E43.MirrorCS"),sQuery(id+"F0.wireOp",EDGE,"E44.MirrorCS"),sQuery(id+"F0.wireOp",EDGE,"E45.MirrorCS"),sQuery(id+"F0.wireOp",EDGE,"E46.MirrorCS"),sQuery(id+"F0.wireOp",EDGE,"E47.MirrorCS"),sQuery(id+"F0.wireOp",EDGE,"E48.MirrorCS"),sQuery(id+"F0.wireOp",EDGE,"E49.MirrorCS"),sQuery(id+"F0.wireOp",EDGE,"E50.MirrorCS"),sQuery(id+"F0.wireOp",EDGE,"E51.MirrorCS"),sQuery(id+"F0.wireOp",EDGE,"E52.MirrorCS")])]});
            transform(context, id + "F14", {"entities" : qUnion([Q0]), "transformType" : TransformType.TRANSLATION_3D, "dx" : 0 * mm, "dy" : 0 * mm, "dz" : 0 * mm, "makeCopy" : true});
        }
    });
